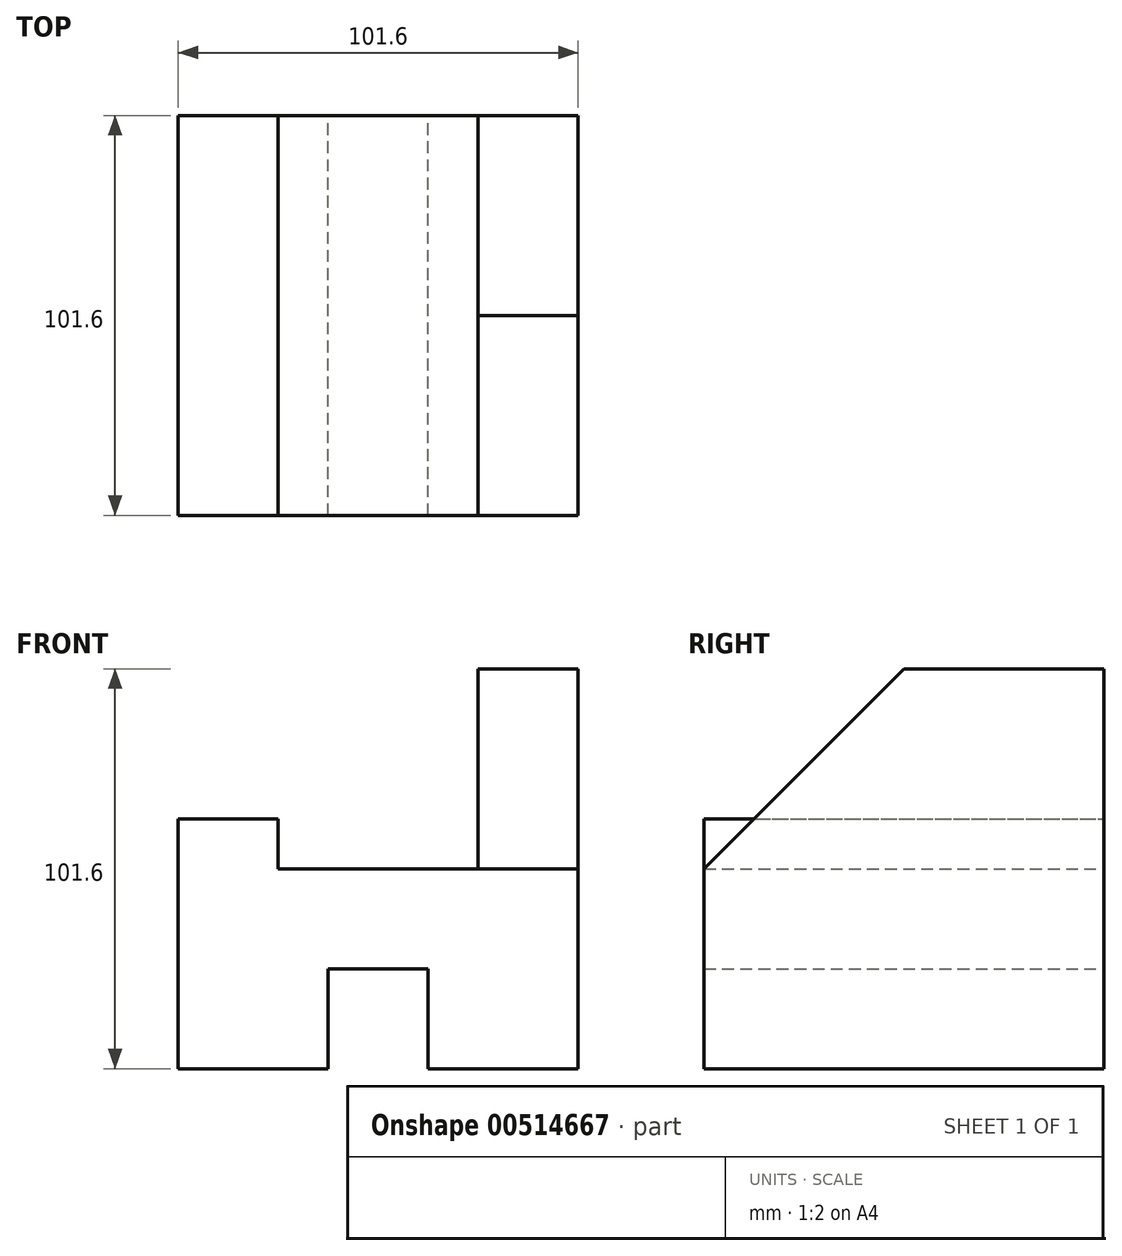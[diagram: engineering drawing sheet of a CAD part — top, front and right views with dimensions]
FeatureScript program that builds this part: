
annotation { "Feature Type Name" : "Feature", "Feature Type Description" : "" }
export const myFeature = defineFeature(function(context is Context, id is Id, definition is map)
    precondition{}
    {
        {
            var Q0;
            Q0=qCreatedBy(makeId("Front.planeOp"),FACE);
            var sketch = newSketch(context, id + "F0", { "sketchPlane" : qUnion([Q0])});
            skLineSegment(sketch, "E0", {"start": v(0, 0) * mm, "end": v(-38.1, 0) * mm});
            skLineSegment(sketch, "E1", {"start": v(-38.1, 0) * mm, "end": v(-38.1, 25.4) * mm});
            skLineSegment(sketch, "E2", {"start": v(-38.1, 25.4) * mm, "end": v(-63.5, 25.4) * mm});
            skLineSegment(sketch, "E3", {"start": v(-63.5, 25.4) * mm, "end": v(-63.5, 0) * mm});
            skLineSegment(sketch, "E4", {"start": v(-63.5, 0) * mm, "end": v(-101.6, 0) * mm});
            skLineSegment(sketch, "E5", {"start": v(-101.6, 0) * mm, "end": v(-101.6, 63.5) * mm});
            skLineSegment(sketch, "E6", {"start": v(-101.6, 63.5) * mm, "end": v(-76.2, 63.5) * mm});
            skLineSegment(sketch, "E7", {"start": v(-76.2, 63.5) * mm, "end": v(-76.2, 50.8) * mm});
            skLineSegment(sketch, "E8", {"start": v(-76.2, 50.8) * mm, "end": v(-25.4, 50.8) * mm});
            skLineSegment(sketch, "E9", {"start": v(-25.4, 50.8) * mm, "end": v(-25.4, 101.6) * mm});
            skLineSegment(sketch, "E10", {"start": v(-25.4, 101.6) * mm, "end": v(0, 101.6) * mm});
            skLineSegment(sketch, "E11", {"start": v(0, 101.6) * mm, "end": v(0, 0) * mm});
            skSolve(sketch);
        }
        {
            var Q0;
            Q0 = qSketchRegion(id + "F0", true);
            extrude(context, id + "F1", {"entities" : qUnion([Q0]), "depth" : 101.6 * mm, "offsetDistance" : 25.4 * mm});
        }
        {
            var Q0;
            Q0=makeQuery(id+"F1.opExtrude","SWEPT_FACE",FACE,{"disambiguationData":[OSD([sQuery(id+"F0.wireOp",EDGE,"E11")])]});
            var sketch = newSketch(context, id + "F2", { "sketchPlane" : qUnion([Q0])});
            skLineSegment(sketch, "E12", {"start": v(-101.6, 50.8) * mm, "end": v(-50.8, 101.6) * mm});
            skSolve(sketch);
        }
        {
            var Q0;
            {var subQ0=sQuery(id+"F2.wireOp",EDGE,"E12");Q0=makeQuery(id+"F2.imprint","IMPRINT",FACE,{"disambiguationData":[TD([[makeQuery(id+"F2.imprint","IMPRINT",EDGE,{"derivedFrom":subQ0}),1.0]])]});}
            extrude(context, id + "F3", {"entities" : qUnion([Q0]), "operationType" : NewBodyOperationType.REMOVE, "oppositeDirection" : true, "depth" : 25.4 * mm, "offsetDistance" : 25.4 * mm});
        }
    });
